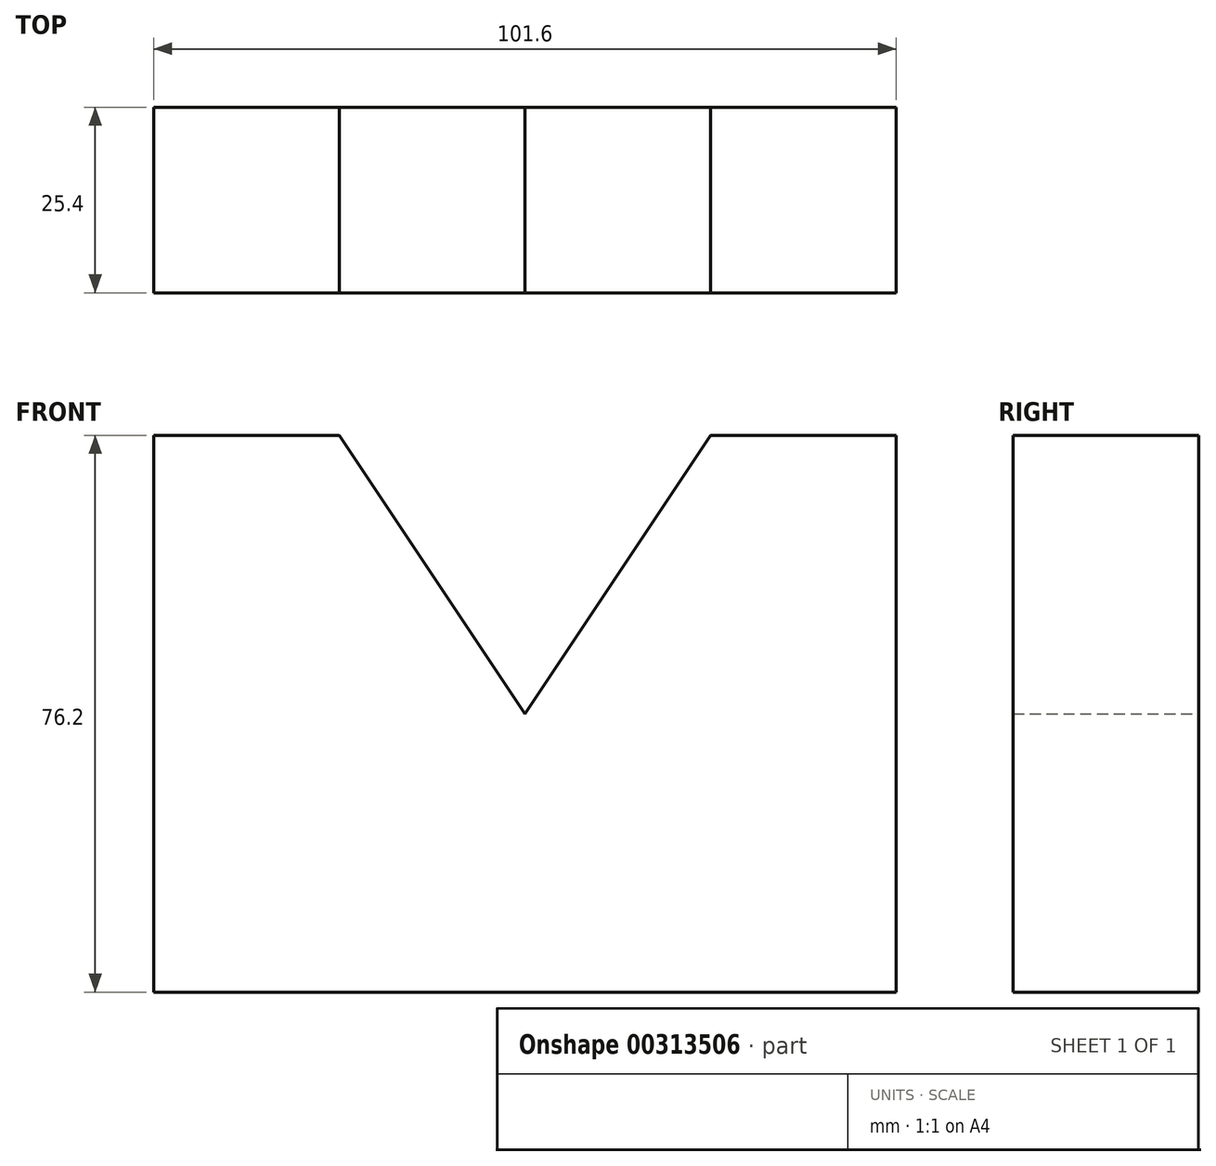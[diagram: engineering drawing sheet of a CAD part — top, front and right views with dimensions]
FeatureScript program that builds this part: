
annotation { "Feature Type Name" : "Feature", "Feature Type Description" : "" }
export const myFeature = defineFeature(function(context is Context, id is Id, definition is map)
    precondition{}
    {
        {
            var Q0;
            Q0=qCreatedBy(makeId("Front.planeOp"),FACE);
            var sketch = newSketch(context, id + "F0", { "sketchPlane" : qUnion([Q0])});
            skLineSegment(sketch, "E0", {"start": v(-49.76, -46.16) * mm, "end": v(51.84, -46.16) * mm});
            skLineSegment(sketch, "E1", {"start": v(51.84, -46.16) * mm, "end": v(51.84, 30.04) * mm});
            skLineSegment(sketch, "E2", {"start": v(-49.76, -46.16) * mm, "end": v(-49.76, 30.04) * mm});
            skLineSegment(sketch, "E3", {"start": v(-49.76, 30.04) * mm, "end": v(-24.36, 30.04) * mm});
            skLineSegment(sketch, "E4", {"start": v(51.84, 30.04) * mm, "end": v(26.44, 30.04) * mm});
            skLineSegment(sketch, "E5", {"start": v(-24.36, 30.04) * mm, "end": v(1.04, -8.06) * mm});
            skLineSegment(sketch, "E6", {"start": v(26.44, 30.04) * mm, "end": v(1.04, -8.06) * mm});
            skSolve(sketch);
        }
        {
            var Q0;
            Q0 = qSketchRegion(id + "F0", true);
            extrude(context, id + "F1", {"entities" : qUnion([Q0]), "depth" : 25.4 * mm});
        }
    });
